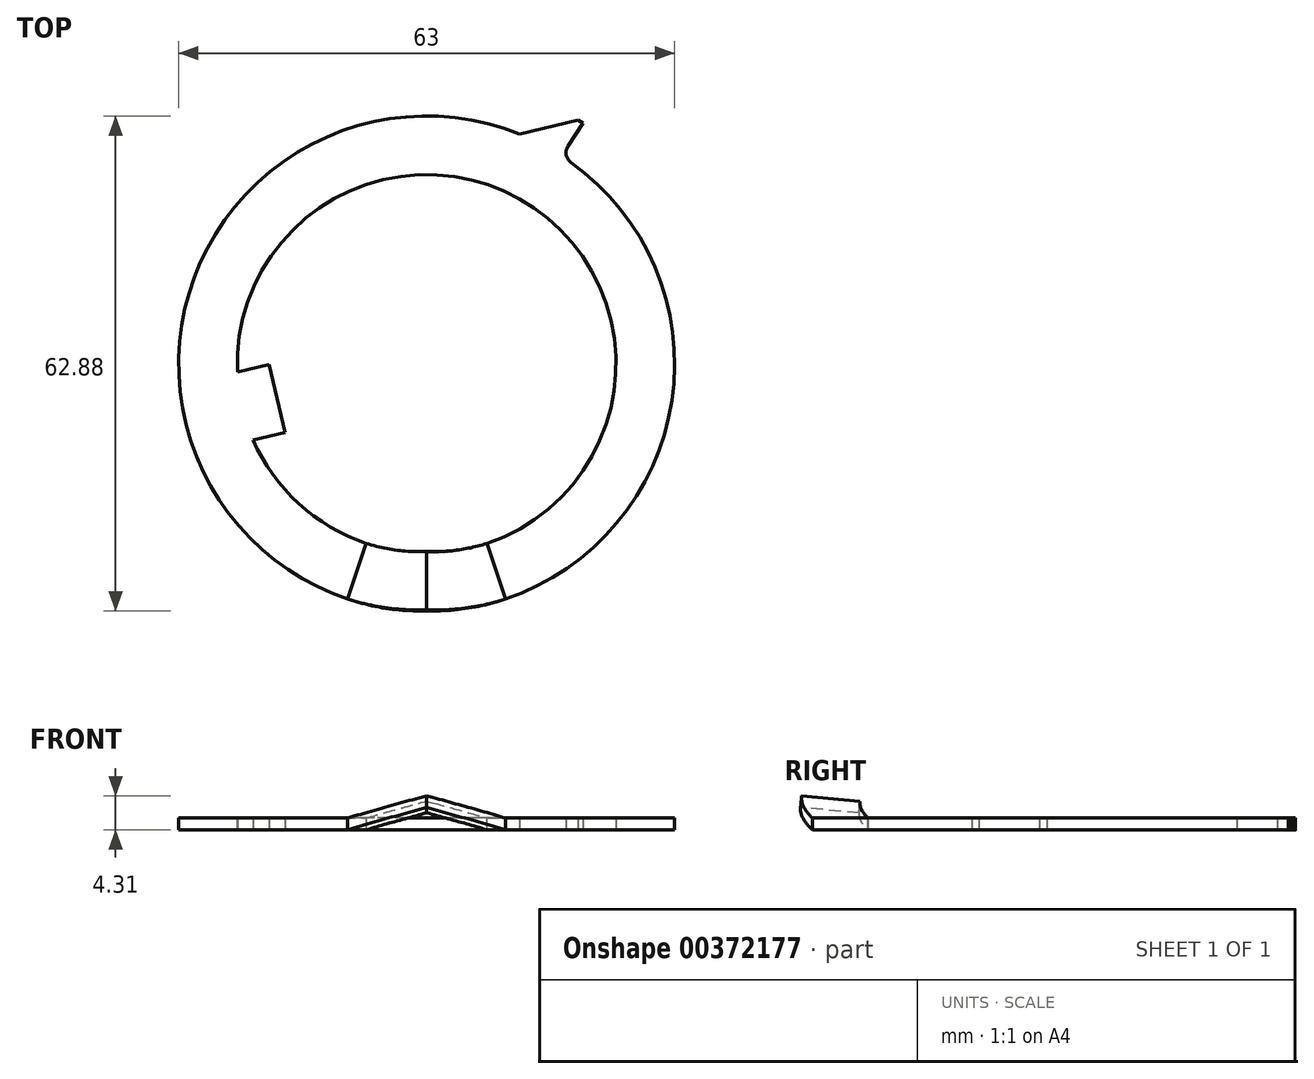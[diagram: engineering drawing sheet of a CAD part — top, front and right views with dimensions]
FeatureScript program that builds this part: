
annotation { "Feature Type Name" : "Feature", "Feature Type Description" : "" }
export const myFeature = defineFeature(function(context is Context, id is Id, definition is map)
    precondition{}
    {
        {
            var Q0;
            Q0=qCreatedBy(makeId("Top.planeOp"),FACE);
            var sketch = newSketch(context, id + "F0", { "sketchPlane" : qUnion([Q0])});
            skArc(sketch, "E0", {"start": v(3.93, 9.74) * mm, "mid": v(-9.85, 3.64) * mm, "end": v(-3.35, -9.95) * mm});
            skArc(sketch, "E1", {"start": v(-7.35, -3.21) * mm, "mid": v(-5.42, -5.91) * mm, "end": v(-2.56, -7.6) * mm});
            skLineSegment(sketch, "E2", {"start": v(0, 0) * mm, "end": v(-6.33, -1.46) * mm, "construction": true});
            skLineSegment(sketch, "E3", {"start": v(-6, -2.9) * mm, "end": v(-6.67, -0.02) * mm});
            skLineSegment(sketch, "E4", {"start": v(-6.67, -0.02) * mm, "end": v(-8.01, -0.34) * mm});
            skLineSegment(sketch, "E5", {"start": v(-6, -2.9) * mm, "end": v(-7.35, -3.21) * mm});
            skLineSegment(sketch, "E6", {"start": v(5.98, 9.22) * mm, "end": v(6.62, 10.2) * mm});
            skLineSegment(sketch, "E7", {"start": v(6.62, 10.2) * mm, "end": v(6.41, 10.33) * mm});
            skLineSegment(sketch, "E8", {"start": v(6.41, 10.33) * mm, "end": v(3.93, 9.74) * mm});
            skLineSegment(sketch, "E9", {"start": v(3.93, 9.74) * mm, "end": v(0, 0) * mm, "construction": true});
            skArc(sketch, "E10", {"start": v(5.98, 9.22) * mm, "mid": v(5.91, 8.85) * mm, "end": v(6.11, 8.54) * mm});
            skLineSegment(sketch, "E11", {"start": v(-2.56, -7.6) * mm, "end": v(-3.35, -9.95) * mm});
            skLineSegment(sketch, "E12", {"start": v(2.56, -7.6) * mm, "end": v(3.35, -9.95) * mm});
            skArc(sketch, "E13.trimOffspring", {"start": v(2.56, -7.6) * mm, "mid": v(4.54, 6.6) * mm, "end": v(-8.01, -0.34) * mm});
            skArc(sketch, "E14.trimOffspring", {"start": v(3.35, -9.95) * mm, "mid": v(10.38, -1.55) * mm, "end": v(6.11, 8.54) * mm});
            skLineSegment(sketch, "E15", {"start": v(0, 0) * mm, "end": v(0, 8.02) * mm, "construction": true});
            skSolve(sketch);
        }
        {
            var Q0;
            Q0=makeQuery(id+"F0.imprint","IMPRINT",FACE,{"disambiguationData":[TD([[makeQuery(id+"F0.imprint","IMPRINT",EDGE,{"derivedFrom":sQuery(id+"F0.wireOp",EDGE,"E0")}),1.0]])]});
            extrude(context, id + "F1", {"entities" : qUnion([Q0]), "depth" : 0.5 * mm});
        }
        {
            var Q0;
            Q0=sQuery(id+"F0.wireOp",EDGE,"E12");
            cPlane(context, id + "F2", {"entities" : qUnion([Q0]), "cplaneType" : CPlaneType.LINE_ANGLE, "offset" : 150 * mm, "angle" : 164.23 * degree, "width" : 150 * mm, "height" : 150 * mm});
        }
        {
            var Q0;
            Q0=qCreatedBy(id+"F2.planeOp",FACE);
            var sketch = newSketch(context, id + "F3", { "sketchPlane" : qUnion([Q0])});
            skArc(sketch, "E16", {"start": v(0, -8) * mm, "mid": v(1.34, -7.89) * mm, "end": v(2.64, -7.55) * mm});
            skArc(sketch, "E17", {"start": v(0, -10.5) * mm, "mid": v(1.76, -10.35) * mm, "end": v(3.47, -9.91) * mm});
            skLineSegment(sketch, "E18", {"start": v(0, 0) * mm, "end": v(0, -10.5) * mm});
            skLineSegment(sketch, "E19", {"start": v(2.64, -7.55) * mm, "end": v(3.47, -9.91) * mm});
            skSolve(sketch);
        }
        {
            var Q0;
            Q0=sQuery(id+"F0.wireOp",EDGE,"E11");
            cPlane(context, id + "F4", {"entities" : qUnion([Q0]), "cplaneType" : CPlaneType.LINE_ANGLE, "offset" : 150 * mm, "angle" : 15.77 * degree, "width" : 150 * mm, "height" : 150 * mm});
        }
        {
            var Q0;
            Q0=qCreatedBy(id+"F4.planeOp",FACE);
            var sketch = newSketch(context, id + "F5", { "sketchPlane" : qUnion([Q0])});
            skArc(sketch, "E20", {"start": v(0, 8) * mm, "mid": v(-1.34, 7.89) * mm, "end": v(-2.64, 7.55) * mm});
            skArc(sketch, "E21", {"start": v(0, 10.5) * mm, "mid": v(-1.76, 10.35) * mm, "end": v(-3.47, 9.91) * mm});
            skLineSegment(sketch, "E22", {"start": v(-3.47, 9.91) * mm, "end": v(-2.64, 7.55) * mm});
            skLineSegment(sketch, "E23", {"start": v(0, 8) * mm, "end": v(0, 10.5) * mm});
            skSolve(sketch);
        }
        {
            var Q0;
            Q0=makeQuery(id+"F1.opExtrude","SWEPT_FACE",FACE,{"disambiguationData":[OSD([sQuery(id+"F0.wireOp",EDGE,"E11")])]});
            var Q1;
            Q1=sQuery(id+"F5.wireOp",EDGE,"E21");
            var Q2;
            Q2=sQuery(id+"F3.wireOp",EDGE,"E17");
            sweep(context, id + "F6", {"operationType" : NewBodyOperationType.ADD, "profiles" : qUnion([Q0]), "path" : qUnion([Q1, Q2])});
        }
        {
            var Q0;
            Q0=makeQuery(id+"F1.opExtrude","SWEPT_BODY",BODY,{"disambiguationData":[OSD([sQuery(id+"F0.wireOp",EDGE,"E0"),sQuery(id+"F0.wireOp",EDGE,"E1"),sQuery(id+"F0.wireOp",EDGE,"E3"),sQuery(id+"F0.wireOp",EDGE,"E4"),sQuery(id+"F0.wireOp",EDGE,"E5"),sQuery(id+"F0.wireOp",EDGE,"E6"),sQuery(id+"F0.wireOp",EDGE,"E7"),sQuery(id+"F0.wireOp",EDGE,"E8"),sQuery(id+"F0.wireOp",EDGE,"E10"),sQuery(id+"F0.wireOp",EDGE,"E11"),sQuery(id+"F0.wireOp",EDGE,"E12"),sQuery(id+"F0.wireOp",EDGE,"E13.trimOffspring"),sQuery(id+"F0.wireOp",EDGE,"E14.trimOffspring")])]});
            var Q1;
            Q1=qCreatedBy(makeId("Origin.pointOp"),VERTEX);
            transform(context, id + "F7", {"entities" : qUnion([Q0]), "transformType" : TransformType.SCALE_UNIFORMLY, "scale" : 3, "makeCopy" : false, "scalePoint" : qUnion([Q1])});
        }
    });
